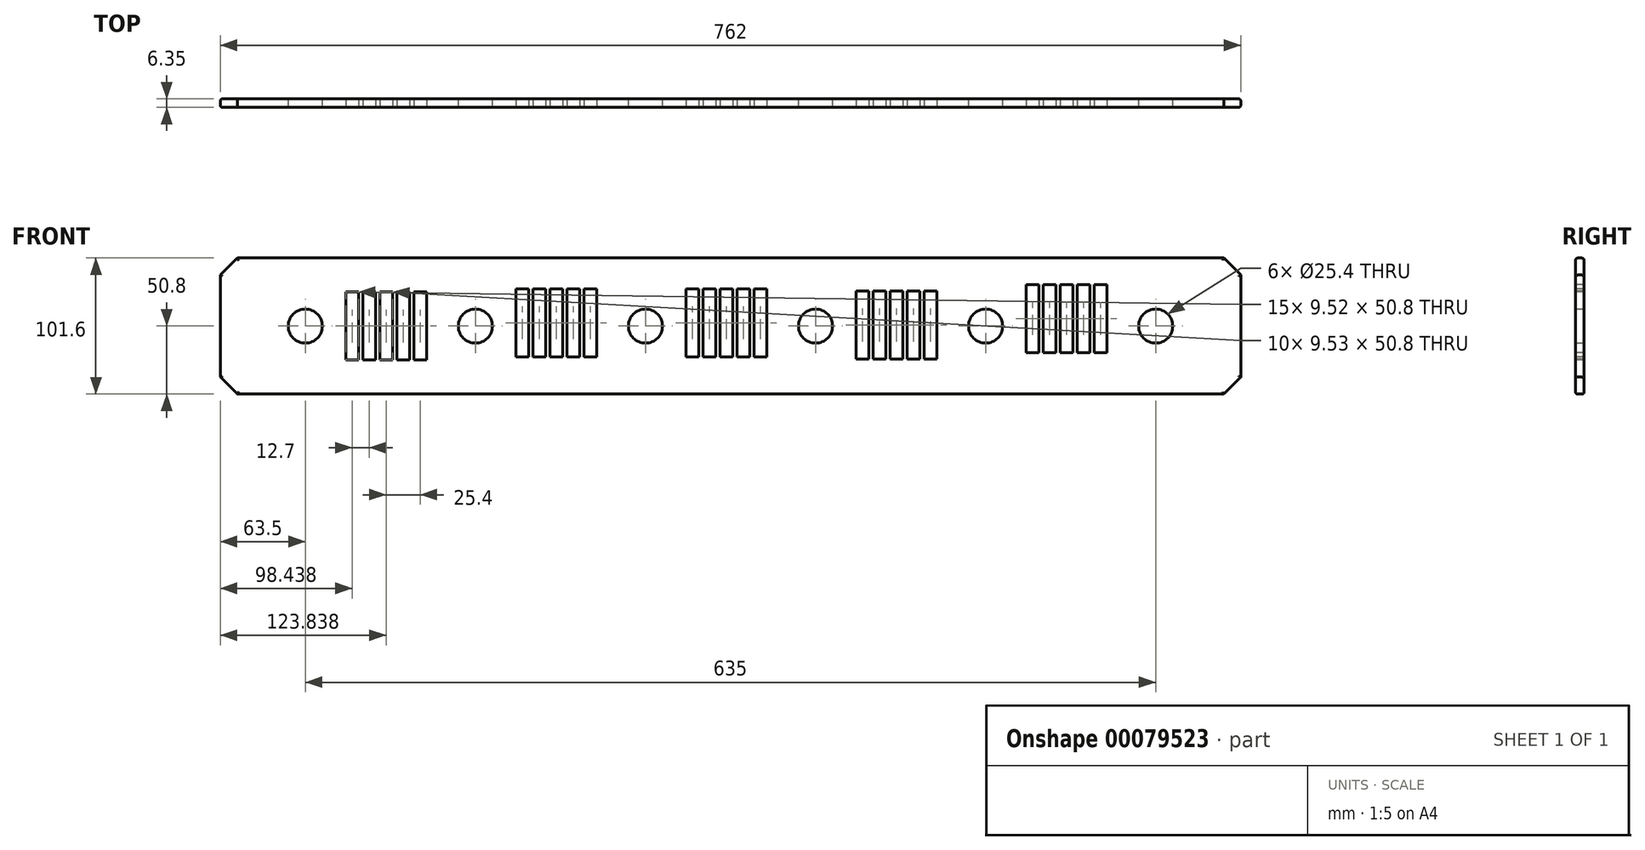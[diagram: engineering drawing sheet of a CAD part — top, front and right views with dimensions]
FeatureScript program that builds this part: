
annotation { "Feature Type Name" : "Feature", "Feature Type Description" : "" }
export const myFeature = defineFeature(function(context is Context, id is Id, definition is map)
    precondition{}
    {
        {
            var Q0;
            Q0=qCreatedBy(makeId("Front.planeOp"),FACE);
            var sketch = newSketch(context, id + "F0", { "sketchPlane" : qUnion([Q0])});
            skLineSegment(sketch, "E0.bottom", {"start": v(0, 0) * mm, "end": v(762, 0) * mm});
            skLineSegment(sketch, "E0.top", {"start": v(0, 101.6) * mm, "end": v(762, 101.6) * mm});
            skLineSegment(sketch, "E0.left", {"start": v(0, 0) * mm, "end": v(0, 101.6) * mm});
            skLineSegment(sketch, "E0.right", {"start": v(762, 0) * mm, "end": v(762, 101.6) * mm});
            skCircle(sketch, "E1", {"center": v(63.5, 50.8) * mm, "radius": 12.7 * mm});
            skPoint(sketch, "E1.centerSnap0", {"position": v(0, 50.8) * mm});
            skCircle(sketch, "E2", {"center": v(190.5, 50.8) * mm, "radius": 12.7 * mm});
            skCircle(sketch, "E3", {"center": v(317.5, 50.8) * mm, "radius": 12.7 * mm});
            skCircle(sketch, "E4", {"center": v(444.5, 50.8) * mm, "radius": 12.7 * mm});
            skCircle(sketch, "E5", {"center": v(571.5, 50.8) * mm, "radius": 12.7 * mm});
            skCircle(sketch, "E6", {"center": v(698.5, 50.8) * mm, "radius": 12.7 * mm});
            skSolve(sketch);
        }
        {
            var Q0;
            Q0=makeQuery(id+"F0.imprint","IMPRINT",FACE,{"disambiguationData":[TD([[makeQuery(id+"F0.imprint","IMPRINT",EDGE,{"derivedFrom":sQuery(id+"F0.wireOp",EDGE,"E0.bottom")}),1.0]])]});
            extrude(context, id + "F1", {"entities" : qUnion([Q0]), "depth" : 6.35 * mm});
        }
        {
            var Q0;
            Q0=makeQuery(id+"F1.opExtrude","CAP_FACE",FACE,{"disambiguationData":[OSD([sQuery(id+"F0.wireOp",EDGE,"E0.bottom"),sQuery(id+"F0.wireOp",EDGE,"E0.top"),sQuery(id+"F0.wireOp",EDGE,"E0.left"),sQuery(id+"F0.wireOp",EDGE,"E0.right"),sQuery(id+"F0.wireOp",EDGE,"E1"),sQuery(id+"F0.wireOp",EDGE,"E2"),sQuery(id+"F0.wireOp",EDGE,"E3"),sQuery(id+"F0.wireOp",EDGE,"E4"),sQuery(id+"F0.wireOp",EDGE,"E5"),sQuery(id+"F0.wireOp",EDGE,"E6")])],"isStart":false});
            var sketch = newSketch(context, id + "F2", { "sketchPlane" : qUnion([Q0])});
            skLineSegment(sketch, "E7.bottom", {"start": v(93.68, 76.2) * mm, "end": v(103.2, 76.2) * mm});
            skLineSegment(sketch, "E7.top", {"start": v(93.68, 25.4) * mm, "end": v(103.2, 25.4) * mm});
            skLineSegment(sketch, "E7.left", {"start": v(93.68, 76.2) * mm, "end": v(93.68, 25.4) * mm});
            skLineSegment(sketch, "E7.right", {"start": v(103.2, 76.2) * mm, "end": v(103.2, 25.4) * mm});
            skLineSegment(sketch, "E8.1.0.0", {"start": v(106.38, 76.2) * mm, "end": v(106.38, 25.4) * mm});
            skLineSegment(sketch, "E8.1.0.1", {"start": v(115.9, 76.2) * mm, "end": v(115.9, 25.4) * mm});
            skLineSegment(sketch, "E8.1.0.2", {"start": v(106.38, 76.2) * mm, "end": v(115.9, 76.2) * mm});
            skLineSegment(sketch, "E8.1.0.3", {"start": v(106.38, 25.4) * mm, "end": v(115.9, 25.4) * mm});
            skLineSegment(sketch, "E8.2.0.0", {"start": v(119.08, 76.2) * mm, "end": v(119.08, 25.4) * mm});
            skLineSegment(sketch, "E8.2.0.1", {"start": v(128.6, 76.2) * mm, "end": v(128.6, 25.4) * mm});
            skLineSegment(sketch, "E8.2.0.2", {"start": v(119.08, 76.2) * mm, "end": v(128.6, 76.2) * mm});
            skLineSegment(sketch, "E8.2.0.3", {"start": v(119.08, 25.4) * mm, "end": v(128.6, 25.4) * mm});
            skLineSegment(sketch, "E8.3.0.0", {"start": v(131.78, 76.2) * mm, "end": v(131.78, 25.4) * mm});
            skLineSegment(sketch, "E8.3.0.1", {"start": v(141.3, 76.2) * mm, "end": v(141.3, 25.4) * mm});
            skLineSegment(sketch, "E8.3.0.2", {"start": v(131.78, 76.2) * mm, "end": v(141.3, 76.2) * mm});
            skLineSegment(sketch, "E8.3.0.3", {"start": v(131.78, 25.4) * mm, "end": v(141.3, 25.4) * mm});
            skLineSegment(sketch, "E8.4.0.0", {"start": v(144.48, 76.2) * mm, "end": v(144.48, 25.4) * mm});
            skLineSegment(sketch, "E8.4.0.1", {"start": v(154, 76.2) * mm, "end": v(154, 25.4) * mm});
            skLineSegment(sketch, "E8.4.0.2", {"start": v(144.48, 76.2) * mm, "end": v(154, 76.2) * mm});
            skLineSegment(sketch, "E8.4.0.3", {"start": v(144.48, 25.4) * mm, "end": v(154, 25.4) * mm});
            skLineSegment(sketch, "E8.direction1", {"start": v(93.68, 25.4) * mm, "end": v(106.38, 25.4) * mm, "construction": true});
            skLineSegment(sketch, "E9.bottom", {"start": v(220.68, 78.71) * mm, "end": v(230.2, 78.71) * mm});
            skLineSegment(sketch, "E9.top", {"start": v(220.68, 27.91) * mm, "end": v(230.2, 27.91) * mm});
            skLineSegment(sketch, "E9.left", {"start": v(220.68, 78.71) * mm, "end": v(220.68, 27.91) * mm});
            skLineSegment(sketch, "E9.right", {"start": v(230.2, 78.71) * mm, "end": v(230.2, 27.91) * mm});
            skLineSegment(sketch, "E10.1.0.0", {"start": v(233.38, 78.71) * mm, "end": v(233.38, 27.91) * mm});
            skLineSegment(sketch, "E10.1.0.1", {"start": v(242.9, 78.71) * mm, "end": v(242.9, 27.91) * mm});
            skLineSegment(sketch, "E10.1.0.2", {"start": v(233.38, 78.71) * mm, "end": v(242.9, 78.71) * mm});
            skLineSegment(sketch, "E10.1.0.3", {"start": v(233.38, 27.91) * mm, "end": v(242.9, 27.91) * mm});
            skLineSegment(sketch, "E10.2.0.0", {"start": v(246.08, 78.71) * mm, "end": v(246.08, 27.91) * mm});
            skLineSegment(sketch, "E10.2.0.1", {"start": v(255.6, 78.71) * mm, "end": v(255.6, 27.91) * mm});
            skLineSegment(sketch, "E10.2.0.2", {"start": v(246.08, 78.71) * mm, "end": v(255.6, 78.71) * mm});
            skLineSegment(sketch, "E10.2.0.3", {"start": v(246.08, 27.91) * mm, "end": v(255.6, 27.91) * mm});
            skLineSegment(sketch, "E10.3.0.0", {"start": v(258.78, 78.71) * mm, "end": v(258.78, 27.91) * mm});
            skLineSegment(sketch, "E10.3.0.1", {"start": v(268.3, 78.71) * mm, "end": v(268.3, 27.91) * mm});
            skLineSegment(sketch, "E10.3.0.2", {"start": v(258.78, 78.71) * mm, "end": v(268.3, 78.71) * mm});
            skLineSegment(sketch, "E10.3.0.3", {"start": v(258.78, 27.91) * mm, "end": v(268.3, 27.91) * mm});
            skLineSegment(sketch, "E10.4.0.0", {"start": v(271.48, 78.71) * mm, "end": v(271.48, 27.91) * mm});
            skLineSegment(sketch, "E10.4.0.1", {"start": v(281, 78.71) * mm, "end": v(281, 27.91) * mm});
            skLineSegment(sketch, "E10.4.0.2", {"start": v(271.48, 78.71) * mm, "end": v(281, 78.71) * mm});
            skLineSegment(sketch, "E10.4.0.3", {"start": v(271.48, 27.91) * mm, "end": v(281, 27.91) * mm});
            skLineSegment(sketch, "E10.direction1", {"start": v(220.68, 27.91) * mm, "end": v(233.38, 27.91) * mm, "construction": true});
            skLineSegment(sketch, "E11.bottom", {"start": v(347.68, 78.67) * mm, "end": v(357.2, 78.67) * mm});
            skLineSegment(sketch, "E11.top", {"start": v(347.68, 27.87) * mm, "end": v(357.2, 27.87) * mm});
            skLineSegment(sketch, "E11.left", {"start": v(347.68, 78.67) * mm, "end": v(347.68, 27.87) * mm});
            skLineSegment(sketch, "E11.right", {"start": v(357.2, 78.67) * mm, "end": v(357.2, 27.87) * mm});
            skLineSegment(sketch, "E12.1.0.0", {"start": v(360.38, 78.67) * mm, "end": v(360.38, 27.87) * mm});
            skLineSegment(sketch, "E12.1.0.1", {"start": v(369.9, 78.67) * mm, "end": v(369.9, 27.87) * mm});
            skLineSegment(sketch, "E12.1.0.2", {"start": v(360.38, 78.67) * mm, "end": v(369.9, 78.67) * mm});
            skLineSegment(sketch, "E12.1.0.3", {"start": v(360.38, 27.87) * mm, "end": v(369.9, 27.87) * mm});
            skLineSegment(sketch, "E12.2.0.0", {"start": v(373.08, 78.67) * mm, "end": v(373.08, 27.87) * mm});
            skLineSegment(sketch, "E12.2.0.1", {"start": v(382.6, 78.67) * mm, "end": v(382.6, 27.87) * mm});
            skLineSegment(sketch, "E12.2.0.2", {"start": v(373.08, 78.67) * mm, "end": v(382.6, 78.67) * mm});
            skLineSegment(sketch, "E12.2.0.3", {"start": v(373.08, 27.87) * mm, "end": v(382.6, 27.87) * mm});
            skLineSegment(sketch, "E12.3.0.0", {"start": v(385.78, 78.67) * mm, "end": v(385.78, 27.87) * mm});
            skLineSegment(sketch, "E12.3.0.1", {"start": v(395.3, 78.67) * mm, "end": v(395.3, 27.87) * mm});
            skLineSegment(sketch, "E12.3.0.2", {"start": v(385.78, 78.67) * mm, "end": v(395.3, 78.67) * mm});
            skLineSegment(sketch, "E12.3.0.3", {"start": v(385.78, 27.87) * mm, "end": v(395.3, 27.87) * mm});
            skLineSegment(sketch, "E12.4.0.0", {"start": v(398.48, 78.67) * mm, "end": v(398.48, 27.87) * mm});
            skLineSegment(sketch, "E12.4.0.1", {"start": v(408, 78.67) * mm, "end": v(408, 27.87) * mm});
            skLineSegment(sketch, "E12.4.0.2", {"start": v(398.48, 78.67) * mm, "end": v(408, 78.67) * mm});
            skLineSegment(sketch, "E12.4.0.3", {"start": v(398.48, 27.87) * mm, "end": v(408, 27.87) * mm});
            skLineSegment(sketch, "E12.direction1", {"start": v(347.68, 27.87) * mm, "end": v(360.38, 27.87) * mm, "construction": true});
            skLineSegment(sketch, "E13.bottom", {"start": v(474.68, 77.02) * mm, "end": v(484.2, 77.02) * mm});
            skLineSegment(sketch, "E13.top", {"start": v(474.68, 26.22) * mm, "end": v(484.2, 26.22) * mm});
            skLineSegment(sketch, "E13.left", {"start": v(474.68, 77.02) * mm, "end": v(474.68, 26.22) * mm});
            skLineSegment(sketch, "E13.right", {"start": v(484.2, 77.02) * mm, "end": v(484.2, 26.22) * mm});
            skLineSegment(sketch, "E14.1.0.0", {"start": v(487.38, 77.02) * mm, "end": v(487.38, 26.22) * mm});
            skLineSegment(sketch, "E14.1.0.1", {"start": v(496.9, 77.02) * mm, "end": v(496.9, 26.22) * mm});
            skLineSegment(sketch, "E14.1.0.2", {"start": v(487.38, 77.02) * mm, "end": v(496.9, 77.02) * mm});
            skLineSegment(sketch, "E14.1.0.3", {"start": v(487.38, 26.22) * mm, "end": v(496.9, 26.22) * mm});
            skLineSegment(sketch, "E14.2.0.0", {"start": v(500.08, 77.02) * mm, "end": v(500.08, 26.22) * mm});
            skLineSegment(sketch, "E14.2.0.1", {"start": v(509.6, 77.02) * mm, "end": v(509.6, 26.22) * mm});
            skLineSegment(sketch, "E14.2.0.2", {"start": v(500.08, 77.02) * mm, "end": v(509.6, 77.02) * mm});
            skLineSegment(sketch, "E14.2.0.3", {"start": v(500.08, 26.22) * mm, "end": v(509.6, 26.22) * mm});
            skLineSegment(sketch, "E14.3.0.0", {"start": v(512.78, 77.02) * mm, "end": v(512.78, 26.22) * mm});
            skLineSegment(sketch, "E14.3.0.1", {"start": v(522.3, 77.02) * mm, "end": v(522.3, 26.22) * mm});
            skLineSegment(sketch, "E14.3.0.2", {"start": v(512.78, 77.02) * mm, "end": v(522.3, 77.02) * mm});
            skLineSegment(sketch, "E14.3.0.3", {"start": v(512.78, 26.22) * mm, "end": v(522.3, 26.22) * mm});
            skLineSegment(sketch, "E14.4.0.0", {"start": v(525.48, 77.02) * mm, "end": v(525.48, 26.22) * mm});
            skLineSegment(sketch, "E14.4.0.1", {"start": v(535, 77.02) * mm, "end": v(535, 26.22) * mm});
            skLineSegment(sketch, "E14.4.0.2", {"start": v(525.48, 77.02) * mm, "end": v(535, 77.02) * mm});
            skLineSegment(sketch, "E14.4.0.3", {"start": v(525.48, 26.22) * mm, "end": v(535, 26.22) * mm});
            skLineSegment(sketch, "E14.direction1", {"start": v(474.68, 26.22) * mm, "end": v(487.38, 26.22) * mm, "construction": true});
            skLineSegment(sketch, "E15.bottom", {"start": v(601.68, 81.85) * mm, "end": v(611.2, 81.85) * mm});
            skLineSegment(sketch, "E15.top", {"start": v(601.68, 31.05) * mm, "end": v(611.2, 31.05) * mm});
            skLineSegment(sketch, "E15.left", {"start": v(601.68, 81.85) * mm, "end": v(601.68, 31.05) * mm});
            skLineSegment(sketch, "E15.right", {"start": v(611.2, 81.85) * mm, "end": v(611.2, 31.05) * mm});
            skLineSegment(sketch, "E16.1.0.0", {"start": v(614.38, 81.85) * mm, "end": v(614.38, 31.05) * mm});
            skLineSegment(sketch, "E16.1.0.1", {"start": v(623.9, 81.85) * mm, "end": v(623.9, 31.05) * mm});
            skLineSegment(sketch, "E16.1.0.2", {"start": v(614.38, 81.85) * mm, "end": v(623.9, 81.85) * mm});
            skLineSegment(sketch, "E16.1.0.3", {"start": v(614.38, 31.05) * mm, "end": v(623.9, 31.05) * mm});
            skLineSegment(sketch, "E16.2.0.0", {"start": v(627.08, 81.85) * mm, "end": v(627.08, 31.05) * mm});
            skLineSegment(sketch, "E16.2.0.1", {"start": v(636.6, 81.85) * mm, "end": v(636.6, 31.05) * mm});
            skLineSegment(sketch, "E16.2.0.2", {"start": v(627.08, 81.85) * mm, "end": v(636.6, 81.85) * mm});
            skLineSegment(sketch, "E16.2.0.3", {"start": v(627.08, 31.05) * mm, "end": v(636.6, 31.05) * mm});
            skLineSegment(sketch, "E16.3.0.0", {"start": v(639.78, 81.85) * mm, "end": v(639.78, 31.05) * mm});
            skLineSegment(sketch, "E16.3.0.1", {"start": v(649.3, 81.85) * mm, "end": v(649.3, 31.05) * mm});
            skLineSegment(sketch, "E16.3.0.2", {"start": v(639.78, 81.85) * mm, "end": v(649.3, 81.85) * mm});
            skLineSegment(sketch, "E16.3.0.3", {"start": v(639.78, 31.05) * mm, "end": v(649.3, 31.05) * mm});
            skLineSegment(sketch, "E16.4.0.0", {"start": v(652.48, 81.85) * mm, "end": v(652.48, 31.05) * mm});
            skLineSegment(sketch, "E16.4.0.1", {"start": v(662, 81.85) * mm, "end": v(662, 31.05) * mm});
            skLineSegment(sketch, "E16.4.0.2", {"start": v(652.48, 81.85) * mm, "end": v(662, 81.85) * mm});
            skLineSegment(sketch, "E16.4.0.3", {"start": v(652.48, 31.05) * mm, "end": v(662, 31.05) * mm});
            skLineSegment(sketch, "E16.direction1", {"start": v(601.68, 31.05) * mm, "end": v(614.38, 31.05) * mm, "construction": true});
            skSolve(sketch);
        }
        {
            var Q0;
            Q0=makeQuery(id+"F2.imprint","IMPRINT",FACE,{"disambiguationData":[TD([[makeQuery(id+"F2.imprint","IMPRINT",EDGE,{"derivedFrom":sQuery(id+"F2.wireOp",EDGE,"E7.bottom")}),-1.0]])]});
            var Q1;
            Q1=makeQuery(id+"F2.imprint","IMPRINT",FACE,{"disambiguationData":[TD([[makeQuery(id+"F2.imprint","IMPRINT",EDGE,{"derivedFrom":sQuery(id+"F2.wireOp",EDGE,"E8.1.0.0")}),1.0]])]});
            var Q2;
            Q2=makeQuery(id+"F2.imprint","IMPRINT",FACE,{"disambiguationData":[TD([[makeQuery(id+"F2.imprint","IMPRINT",EDGE,{"derivedFrom":sQuery(id+"F2.wireOp",EDGE,"E8.2.0.0")}),1.0]])]});
            var Q3;
            Q3=makeQuery(id+"F2.imprint","IMPRINT",FACE,{"disambiguationData":[TD([[makeQuery(id+"F2.imprint","IMPRINT",EDGE,{"derivedFrom":sQuery(id+"F2.wireOp",EDGE,"E8.3.0.0")}),1.0]])]});
            var Q4;
            Q4=makeQuery(id+"F2.imprint","IMPRINT",FACE,{"disambiguationData":[TD([[makeQuery(id+"F2.imprint","IMPRINT",EDGE,{"derivedFrom":sQuery(id+"F2.wireOp",EDGE,"E8.4.0.0")}),1.0]])]});
            var Q5;
            Q5=makeQuery(id+"F2.imprint","IMPRINT",FACE,{"disambiguationData":[TD([[makeQuery(id+"F2.imprint","IMPRINT",EDGE,{"derivedFrom":sQuery(id+"F2.wireOp",EDGE,"E9.bottom")}),-1.0]])]});
            var Q6;
            Q6=makeQuery(id+"F2.imprint","IMPRINT",FACE,{"disambiguationData":[TD([[makeQuery(id+"F2.imprint","IMPRINT",EDGE,{"derivedFrom":sQuery(id+"F2.wireOp",EDGE,"E10.1.0.0")}),1.0]])]});
            var Q7;
            Q7=makeQuery(id+"F2.imprint","IMPRINT",FACE,{"disambiguationData":[TD([[makeQuery(id+"F2.imprint","IMPRINT",EDGE,{"derivedFrom":sQuery(id+"F2.wireOp",EDGE,"E10.2.0.0")}),1.0]])]});
            var Q8;
            Q8=makeQuery(id+"F2.imprint","IMPRINT",FACE,{"disambiguationData":[TD([[makeQuery(id+"F2.imprint","IMPRINT",EDGE,{"derivedFrom":sQuery(id+"F2.wireOp",EDGE,"E10.3.0.0")}),1.0]])]});
            var Q9;
            Q9=makeQuery(id+"F2.imprint","IMPRINT",FACE,{"disambiguationData":[TD([[makeQuery(id+"F2.imprint","IMPRINT",EDGE,{"derivedFrom":sQuery(id+"F2.wireOp",EDGE,"E10.4.0.0")}),1.0]])]});
            var Q10;
            Q10=makeQuery(id+"F2.imprint","IMPRINT",FACE,{"disambiguationData":[TD([[makeQuery(id+"F2.imprint","IMPRINT",EDGE,{"derivedFrom":sQuery(id+"F2.wireOp",EDGE,"E11.bottom")}),-1.0]])]});
            var Q11;
            Q11=makeQuery(id+"F2.imprint","IMPRINT",FACE,{"disambiguationData":[TD([[makeQuery(id+"F2.imprint","IMPRINT",EDGE,{"derivedFrom":sQuery(id+"F2.wireOp",EDGE,"E12.1.0.0")}),1.0]])]});
            var Q12;
            Q12=makeQuery(id+"F2.imprint","IMPRINT",FACE,{"disambiguationData":[TD([[makeQuery(id+"F2.imprint","IMPRINT",EDGE,{"derivedFrom":sQuery(id+"F2.wireOp",EDGE,"E12.2.0.0")}),1.0]])]});
            var Q13;
            Q13=makeQuery(id+"F2.imprint","IMPRINT",FACE,{"disambiguationData":[TD([[makeQuery(id+"F2.imprint","IMPRINT",EDGE,{"derivedFrom":sQuery(id+"F2.wireOp",EDGE,"E12.3.0.0")}),1.0]])]});
            var Q14;
            Q14=makeQuery(id+"F2.imprint","IMPRINT",FACE,{"disambiguationData":[TD([[makeQuery(id+"F2.imprint","IMPRINT",EDGE,{"derivedFrom":sQuery(id+"F2.wireOp",EDGE,"E12.4.0.0")}),1.0]])]});
            var Q15;
            Q15=makeQuery(id+"F2.imprint","IMPRINT",FACE,{"disambiguationData":[TD([[makeQuery(id+"F2.imprint","IMPRINT",EDGE,{"derivedFrom":sQuery(id+"F2.wireOp",EDGE,"E13.bottom")}),-1.0]])]});
            var Q16;
            Q16=makeQuery(id+"F2.imprint","IMPRINT",FACE,{"disambiguationData":[TD([[makeQuery(id+"F2.imprint","IMPRINT",EDGE,{"derivedFrom":sQuery(id+"F2.wireOp",EDGE,"E14.1.0.0")}),1.0]])]});
            var Q17;
            Q17=makeQuery(id+"F2.imprint","IMPRINT",FACE,{"disambiguationData":[TD([[makeQuery(id+"F2.imprint","IMPRINT",EDGE,{"derivedFrom":sQuery(id+"F2.wireOp",EDGE,"E14.2.0.0")}),1.0]])]});
            var Q18;
            Q18=makeQuery(id+"F2.imprint","IMPRINT",FACE,{"disambiguationData":[TD([[makeQuery(id+"F2.imprint","IMPRINT",EDGE,{"derivedFrom":sQuery(id+"F2.wireOp",EDGE,"E14.3.0.0")}),1.0]])]});
            var Q19;
            Q19=makeQuery(id+"F2.imprint","IMPRINT",FACE,{"disambiguationData":[TD([[makeQuery(id+"F2.imprint","IMPRINT",EDGE,{"derivedFrom":sQuery(id+"F2.wireOp",EDGE,"E14.4.0.0")}),1.0]])]});
            var Q20;
            Q20=makeQuery(id+"F2.imprint","IMPRINT",FACE,{"disambiguationData":[TD([[makeQuery(id+"F2.imprint","IMPRINT",EDGE,{"derivedFrom":sQuery(id+"F2.wireOp",EDGE,"E15.bottom")}),-1.0]])]});
            var Q21;
            Q21=makeQuery(id+"F2.imprint","IMPRINT",FACE,{"disambiguationData":[TD([[makeQuery(id+"F2.imprint","IMPRINT",EDGE,{"derivedFrom":sQuery(id+"F2.wireOp",EDGE,"E16.1.0.0")}),1.0]])]});
            var Q22;
            Q22=makeQuery(id+"F2.imprint","IMPRINT",FACE,{"disambiguationData":[TD([[makeQuery(id+"F2.imprint","IMPRINT",EDGE,{"derivedFrom":sQuery(id+"F2.wireOp",EDGE,"E16.2.0.0")}),1.0]])]});
            var Q23;
            Q23=makeQuery(id+"F2.imprint","IMPRINT",FACE,{"disambiguationData":[TD([[makeQuery(id+"F2.imprint","IMPRINT",EDGE,{"derivedFrom":sQuery(id+"F2.wireOp",EDGE,"E16.3.0.0")}),1.0]])]});
            var Q24;
            Q24=makeQuery(id+"F2.imprint","IMPRINT",FACE,{"disambiguationData":[TD([[makeQuery(id+"F2.imprint","IMPRINT",EDGE,{"derivedFrom":sQuery(id+"F2.wireOp",EDGE,"E16.4.0.0")}),1.0]])]});
            extrude(context, id + "F3", {"entities" : qUnion([Q0, Q1, Q2, Q3, Q4, Q5, Q6, Q7, Q8, Q9, Q10, Q11, Q12, Q13, Q14, Q15, Q16, Q17, Q18, Q19, Q20, Q21, Q22, Q23, Q24]), "operationType" : NewBodyOperationType.REMOVE, "endBound" : BoundingType.THROUGH_ALL, "oppositeDirection" : true, "depth" : 25.4 * mm});
        }
        {
            var Q0;
            Q0=makeQuery(id+"F1.opExtrude","SWEPT_EDGE",EDGE,{"disambiguationData":[OSD([sQuery(id+"F0.wireOp",EDGE,"E0.top"),sQuery(id+"F0.wireOp",EDGE,"E0.left")])]});
            var Q1;
            Q1=makeQuery(id+"F1.opExtrude","SWEPT_EDGE",EDGE,{"disambiguationData":[OSD([sQuery(id+"F0.wireOp",EDGE,"E0.bottom"),sQuery(id+"F0.wireOp",EDGE,"E0.left")])]});
            var Q2;
            Q2=makeQuery(id+"F1.opExtrude","SWEPT_EDGE",EDGE,{"disambiguationData":[OSD([sQuery(id+"F0.wireOp",EDGE,"E0.bottom"),sQuery(id+"F0.wireOp",EDGE,"E0.right")])]});
            var Q3;
            Q3=makeQuery(id+"F1.opExtrude","SWEPT_EDGE",EDGE,{"disambiguationData":[OSD([sQuery(id+"F0.wireOp",EDGE,"E0.top"),sQuery(id+"F0.wireOp",EDGE,"E0.right")])]});
            chamfer(context, id + "F4", {"entities" : qUnion([Q0, Q1, Q2, Q3]), "width" : 12.7 * mm, "tangentPropagation" : true});
        }
        {
            var Q0;
            Q0=makeQuery(id+"F1.opExtrude","CAP_EDGE",EDGE,{"disambiguationData":[OSD([sQuery(id+"F0.wireOp",EDGE,"E0.top")])],"isStart":false});
            var Q1;
            Q1=makeQuery(id+"F1.opExtrude","CAP_EDGE",EDGE,{"disambiguationData":[OSD([sQuery(id+"F0.wireOp",EDGE,"E0.top")])],"isStart":true});
            var Q2;
            {var subQ0=sQuery(id+"F0.wireOp",EDGE,"E0.left");var subQ1=sQuery(id+"F0.wireOp",EDGE,"E0.top");Q2=makeQuery(id+"F4.opChamfer","BLEND_EDGE",EDGE,{"blendedFrom":[makeQuery(id+"F1.opExtrude","SWEPT_EDGE",EDGE,{"disambiguationData":[OSD([subQ1,subQ0])]}),makeQuery(id+"F1.opExtrude","CAP_FACE",FACE,{"disambiguationData":[OSD([sQuery(id+"F0.wireOp",EDGE,"E0.bottom"),subQ1,subQ0,sQuery(id+"F0.wireOp",EDGE,"E0.right"),sQuery(id+"F0.wireOp",EDGE,"E1"),sQuery(id+"F0.wireOp",EDGE,"E2"),sQuery(id+"F0.wireOp",EDGE,"E3"),sQuery(id+"F0.wireOp",EDGE,"E4"),sQuery(id+"F0.wireOp",EDGE,"E5"),sQuery(id+"F0.wireOp",EDGE,"E6")])],"isStart":false})],"blendedInto":[makeQuery(id+"F1.opExtrude","CAP_FACE",FACE,{"disambiguationData":[OSD([sQuery(id+"F0.wireOp",EDGE,"E0.bottom"),subQ1,subQ0,sQuery(id+"F0.wireOp",EDGE,"E0.right"),sQuery(id+"F0.wireOp",EDGE,"E1"),sQuery(id+"F0.wireOp",EDGE,"E2"),sQuery(id+"F0.wireOp",EDGE,"E3"),sQuery(id+"F0.wireOp",EDGE,"E4"),sQuery(id+"F0.wireOp",EDGE,"E5"),sQuery(id+"F0.wireOp",EDGE,"E6")])],"isStart":false})]});}
            var Q3;
            {var subQ0=sQuery(id+"F0.wireOp",EDGE,"E0.left");var subQ1=sQuery(id+"F0.wireOp",EDGE,"E0.top");Q3=makeQuery(id+"F4.opChamfer","BLEND_EDGE",EDGE,{"blendedFrom":[makeQuery(id+"F1.opExtrude","SWEPT_EDGE",EDGE,{"disambiguationData":[OSD([subQ1,subQ0])]}),makeQuery(id+"F1.opExtrude","CAP_FACE",FACE,{"disambiguationData":[OSD([sQuery(id+"F0.wireOp",EDGE,"E0.bottom"),subQ1,subQ0,sQuery(id+"F0.wireOp",EDGE,"E0.right"),sQuery(id+"F0.wireOp",EDGE,"E1"),sQuery(id+"F0.wireOp",EDGE,"E2"),sQuery(id+"F0.wireOp",EDGE,"E3"),sQuery(id+"F0.wireOp",EDGE,"E4"),sQuery(id+"F0.wireOp",EDGE,"E5"),sQuery(id+"F0.wireOp",EDGE,"E6")])],"isStart":true})],"blendedInto":[makeQuery(id+"F1.opExtrude","CAP_FACE",FACE,{"disambiguationData":[OSD([sQuery(id+"F0.wireOp",EDGE,"E0.bottom"),subQ1,subQ0,sQuery(id+"F0.wireOp",EDGE,"E0.right"),sQuery(id+"F0.wireOp",EDGE,"E1"),sQuery(id+"F0.wireOp",EDGE,"E2"),sQuery(id+"F0.wireOp",EDGE,"E3"),sQuery(id+"F0.wireOp",EDGE,"E4"),sQuery(id+"F0.wireOp",EDGE,"E5"),sQuery(id+"F0.wireOp",EDGE,"E6")])],"isStart":true})]});}
            var Q4;
            Q4=makeQuery(id+"F1.opExtrude","CAP_EDGE",EDGE,{"disambiguationData":[OSD([sQuery(id+"F0.wireOp",EDGE,"E0.left")])],"isStart":false});
            var Q5;
            Q5=makeQuery(id+"F1.opExtrude","CAP_EDGE",EDGE,{"disambiguationData":[OSD([sQuery(id+"F0.wireOp",EDGE,"E0.left")])],"isStart":true});
            var Q6;
            {var subQ0=sQuery(id+"F0.wireOp",EDGE,"E0.left");var subQ1=sQuery(id+"F0.wireOp",EDGE,"E0.bottom");Q6=makeQuery(id+"F4.opChamfer","BLEND_EDGE",EDGE,{"blendedFrom":[makeQuery(id+"F1.opExtrude","SWEPT_EDGE",EDGE,{"disambiguationData":[OSD([subQ1,subQ0])]}),makeQuery(id+"F1.opExtrude","CAP_FACE",FACE,{"disambiguationData":[OSD([subQ1,sQuery(id+"F0.wireOp",EDGE,"E0.top"),subQ0,sQuery(id+"F0.wireOp",EDGE,"E0.right"),sQuery(id+"F0.wireOp",EDGE,"E1"),sQuery(id+"F0.wireOp",EDGE,"E2"),sQuery(id+"F0.wireOp",EDGE,"E3"),sQuery(id+"F0.wireOp",EDGE,"E4"),sQuery(id+"F0.wireOp",EDGE,"E5"),sQuery(id+"F0.wireOp",EDGE,"E6")])],"isStart":false})],"blendedInto":[makeQuery(id+"F1.opExtrude","CAP_FACE",FACE,{"disambiguationData":[OSD([subQ1,sQuery(id+"F0.wireOp",EDGE,"E0.top"),subQ0,sQuery(id+"F0.wireOp",EDGE,"E0.right"),sQuery(id+"F0.wireOp",EDGE,"E1"),sQuery(id+"F0.wireOp",EDGE,"E2"),sQuery(id+"F0.wireOp",EDGE,"E3"),sQuery(id+"F0.wireOp",EDGE,"E4"),sQuery(id+"F0.wireOp",EDGE,"E5"),sQuery(id+"F0.wireOp",EDGE,"E6")])],"isStart":false})]});}
            var Q7;
            {var subQ0=sQuery(id+"F0.wireOp",EDGE,"E0.left");var subQ1=sQuery(id+"F0.wireOp",EDGE,"E0.bottom");Q7=makeQuery(id+"F4.opChamfer","BLEND_EDGE",EDGE,{"blendedFrom":[makeQuery(id+"F1.opExtrude","SWEPT_EDGE",EDGE,{"disambiguationData":[OSD([subQ1,subQ0])]}),makeQuery(id+"F1.opExtrude","CAP_FACE",FACE,{"disambiguationData":[OSD([subQ1,sQuery(id+"F0.wireOp",EDGE,"E0.top"),subQ0,sQuery(id+"F0.wireOp",EDGE,"E0.right"),sQuery(id+"F0.wireOp",EDGE,"E1"),sQuery(id+"F0.wireOp",EDGE,"E2"),sQuery(id+"F0.wireOp",EDGE,"E3"),sQuery(id+"F0.wireOp",EDGE,"E4"),sQuery(id+"F0.wireOp",EDGE,"E5"),sQuery(id+"F0.wireOp",EDGE,"E6")])],"isStart":true})],"blendedInto":[makeQuery(id+"F1.opExtrude","CAP_FACE",FACE,{"disambiguationData":[OSD([subQ1,sQuery(id+"F0.wireOp",EDGE,"E0.top"),subQ0,sQuery(id+"F0.wireOp",EDGE,"E0.right"),sQuery(id+"F0.wireOp",EDGE,"E1"),sQuery(id+"F0.wireOp",EDGE,"E2"),sQuery(id+"F0.wireOp",EDGE,"E3"),sQuery(id+"F0.wireOp",EDGE,"E4"),sQuery(id+"F0.wireOp",EDGE,"E5"),sQuery(id+"F0.wireOp",EDGE,"E6")])],"isStart":true})]});}
            var Q8;
            Q8=makeQuery(id+"F1.opExtrude","CAP_EDGE",EDGE,{"disambiguationData":[OSD([sQuery(id+"F0.wireOp",EDGE,"E0.bottom")])],"isStart":false});
            var Q9;
            Q9=makeQuery(id+"F1.opExtrude","CAP_EDGE",EDGE,{"disambiguationData":[OSD([sQuery(id+"F0.wireOp",EDGE,"E0.bottom")])],"isStart":true});
            var Q10;
            {var subQ0=sQuery(id+"F0.wireOp",EDGE,"E0.right");var subQ1=sQuery(id+"F0.wireOp",EDGE,"E0.top");Q10=makeQuery(id+"F4.opChamfer","BLEND_EDGE",EDGE,{"blendedFrom":[makeQuery(id+"F1.opExtrude","SWEPT_EDGE",EDGE,{"disambiguationData":[OSD([subQ1,subQ0])]}),makeQuery(id+"F1.opExtrude","CAP_FACE",FACE,{"disambiguationData":[OSD([sQuery(id+"F0.wireOp",EDGE,"E0.bottom"),subQ1,sQuery(id+"F0.wireOp",EDGE,"E0.left"),subQ0,sQuery(id+"F0.wireOp",EDGE,"E1"),sQuery(id+"F0.wireOp",EDGE,"E2"),sQuery(id+"F0.wireOp",EDGE,"E3"),sQuery(id+"F0.wireOp",EDGE,"E4"),sQuery(id+"F0.wireOp",EDGE,"E5"),sQuery(id+"F0.wireOp",EDGE,"E6")])],"isStart":false})],"blendedInto":[makeQuery(id+"F1.opExtrude","CAP_FACE",FACE,{"disambiguationData":[OSD([sQuery(id+"F0.wireOp",EDGE,"E0.bottom"),subQ1,sQuery(id+"F0.wireOp",EDGE,"E0.left"),subQ0,sQuery(id+"F0.wireOp",EDGE,"E1"),sQuery(id+"F0.wireOp",EDGE,"E2"),sQuery(id+"F0.wireOp",EDGE,"E3"),sQuery(id+"F0.wireOp",EDGE,"E4"),sQuery(id+"F0.wireOp",EDGE,"E5"),sQuery(id+"F0.wireOp",EDGE,"E6")])],"isStart":false})]});}
            var Q11;
            {var subQ0=sQuery(id+"F0.wireOp",EDGE,"E0.right");var subQ1=sQuery(id+"F0.wireOp",EDGE,"E0.top");Q11=makeQuery(id+"F4.opChamfer","BLEND_EDGE",EDGE,{"blendedFrom":[makeQuery(id+"F1.opExtrude","SWEPT_EDGE",EDGE,{"disambiguationData":[OSD([subQ1,subQ0])]}),makeQuery(id+"F1.opExtrude","CAP_FACE",FACE,{"disambiguationData":[OSD([sQuery(id+"F0.wireOp",EDGE,"E0.bottom"),subQ1,sQuery(id+"F0.wireOp",EDGE,"E0.left"),subQ0,sQuery(id+"F0.wireOp",EDGE,"E1"),sQuery(id+"F0.wireOp",EDGE,"E2"),sQuery(id+"F0.wireOp",EDGE,"E3"),sQuery(id+"F0.wireOp",EDGE,"E4"),sQuery(id+"F0.wireOp",EDGE,"E5"),sQuery(id+"F0.wireOp",EDGE,"E6")])],"isStart":true})],"blendedInto":[makeQuery(id+"F1.opExtrude","CAP_FACE",FACE,{"disambiguationData":[OSD([sQuery(id+"F0.wireOp",EDGE,"E0.bottom"),subQ1,sQuery(id+"F0.wireOp",EDGE,"E0.left"),subQ0,sQuery(id+"F0.wireOp",EDGE,"E1"),sQuery(id+"F0.wireOp",EDGE,"E2"),sQuery(id+"F0.wireOp",EDGE,"E3"),sQuery(id+"F0.wireOp",EDGE,"E4"),sQuery(id+"F0.wireOp",EDGE,"E5"),sQuery(id+"F0.wireOp",EDGE,"E6")])],"isStart":true})]});}
            var Q12;
            Q12=makeQuery(id+"F1.opExtrude","CAP_EDGE",EDGE,{"disambiguationData":[OSD([sQuery(id+"F0.wireOp",EDGE,"E0.right")])],"isStart":true});
            var Q13;
            Q13=makeQuery(id+"F1.opExtrude","CAP_EDGE",EDGE,{"disambiguationData":[OSD([sQuery(id+"F0.wireOp",EDGE,"E0.right")])],"isStart":false});
            var Q14;
            {var subQ0=sQuery(id+"F0.wireOp",EDGE,"E0.right");var subQ1=sQuery(id+"F0.wireOp",EDGE,"E0.bottom");Q14=makeQuery(id+"F4.opChamfer","BLEND_EDGE",EDGE,{"blendedFrom":[makeQuery(id+"F1.opExtrude","SWEPT_EDGE",EDGE,{"disambiguationData":[OSD([subQ1,subQ0])]}),makeQuery(id+"F1.opExtrude","CAP_FACE",FACE,{"disambiguationData":[OSD([subQ1,sQuery(id+"F0.wireOp",EDGE,"E0.top"),sQuery(id+"F0.wireOp",EDGE,"E0.left"),subQ0,sQuery(id+"F0.wireOp",EDGE,"E1"),sQuery(id+"F0.wireOp",EDGE,"E2"),sQuery(id+"F0.wireOp",EDGE,"E3"),sQuery(id+"F0.wireOp",EDGE,"E4"),sQuery(id+"F0.wireOp",EDGE,"E5"),sQuery(id+"F0.wireOp",EDGE,"E6")])],"isStart":false})],"blendedInto":[makeQuery(id+"F1.opExtrude","CAP_FACE",FACE,{"disambiguationData":[OSD([subQ1,sQuery(id+"F0.wireOp",EDGE,"E0.top"),sQuery(id+"F0.wireOp",EDGE,"E0.left"),subQ0,sQuery(id+"F0.wireOp",EDGE,"E1"),sQuery(id+"F0.wireOp",EDGE,"E2"),sQuery(id+"F0.wireOp",EDGE,"E3"),sQuery(id+"F0.wireOp",EDGE,"E4"),sQuery(id+"F0.wireOp",EDGE,"E5"),sQuery(id+"F0.wireOp",EDGE,"E6")])],"isStart":false})]});}
            fillet(context, id + "F5", {"entities" : qUnion([Q0, Q1, Q2, Q3, Q4, Q5, Q6, Q7, Q8, Q9, Q10, Q11, Q12, Q13, Q14]), "radius" : 1.6 * mm, "tangentPropagation" : true, "allowEdgeOverflow" : false});
        }
    });
